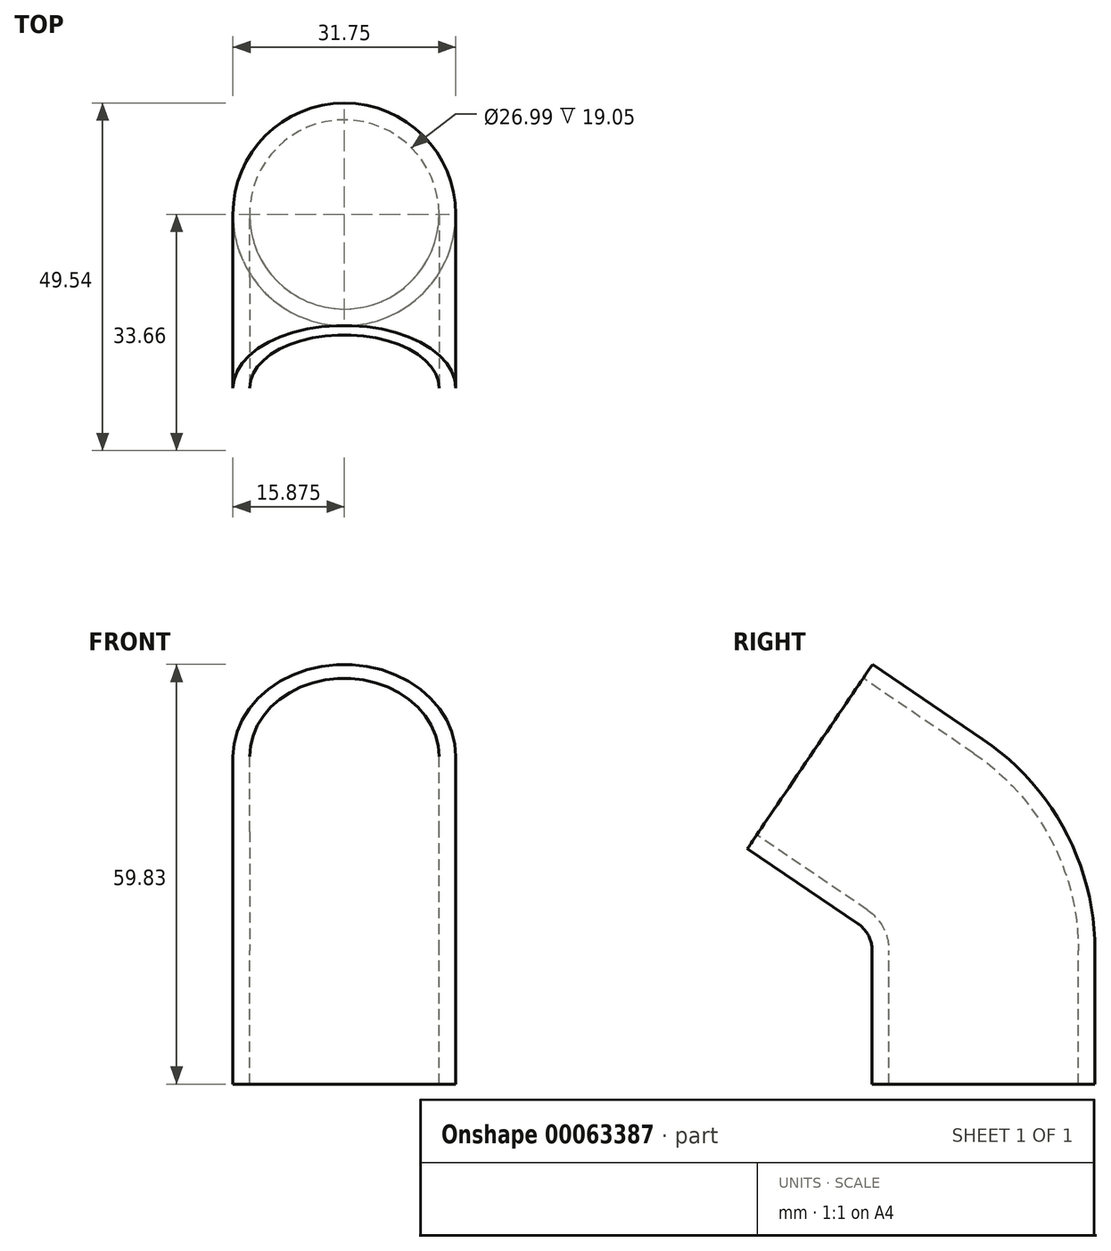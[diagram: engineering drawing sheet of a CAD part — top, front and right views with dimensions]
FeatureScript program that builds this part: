
annotation { "Feature Type Name" : "Feature", "Feature Type Description" : "" }
export const myFeature = defineFeature(function(context is Context, id is Id, definition is map)
    precondition{}
    {
        {
            var Q0;
            Q0=qCreatedBy(makeId("Top.planeOp"),FACE);
            var sketch = newSketch(context, id + "F0", { "sketchPlane" : qUnion([Q0])});
            skCircle(sketch, "E0", {"center": v(15.88, 0) * mm, "radius": 15.88 * mm});
            skCircle(sketch, "E1", {"center": v(15.88, 0) * mm, "radius": 13.5 * mm});
            skSolve(sketch);
        }
        {
            var Q0;
            Q0=qCreatedBy(makeId("Right.planeOp"),FACE);
            var sketch = newSketch(context, id + "F1", { "sketchPlane" : qUnion([Q0])});
            skLineSegment(sketch, "E2", {"start": v(0, 0) * mm, "end": v(0, 19.05) * mm});
            skLineSegment(sketch, "E3", {"start": v(-8.98, 36) * mm, "end": v(-24.74, 46.7) * mm});
            skArc(sketch, "E4", {"start": v(0, 19.05) * mm, "mid": v(-2.38, 28.64) * mm, "end": v(-8.98, 36) * mm});
            skSolve(sketch);
        }
        {
            var Q0;
            Q0 = qSketchRegion(id + "F0", true);
            var Q1;
            Q1=sQuery(id+"F1.wireOp",EDGE,"E2");
            var Q2;
            Q2=sQuery(id+"F1.wireOp",EDGE,"E4");
            var Q3;
            Q3=sQuery(id+"F1.wireOp",EDGE,"E3");
            sweep(context, id + "F2", {"profiles" : qUnion([Q0]), "path" : qUnion([Q1, Q2, Q3])});
        }
    });
